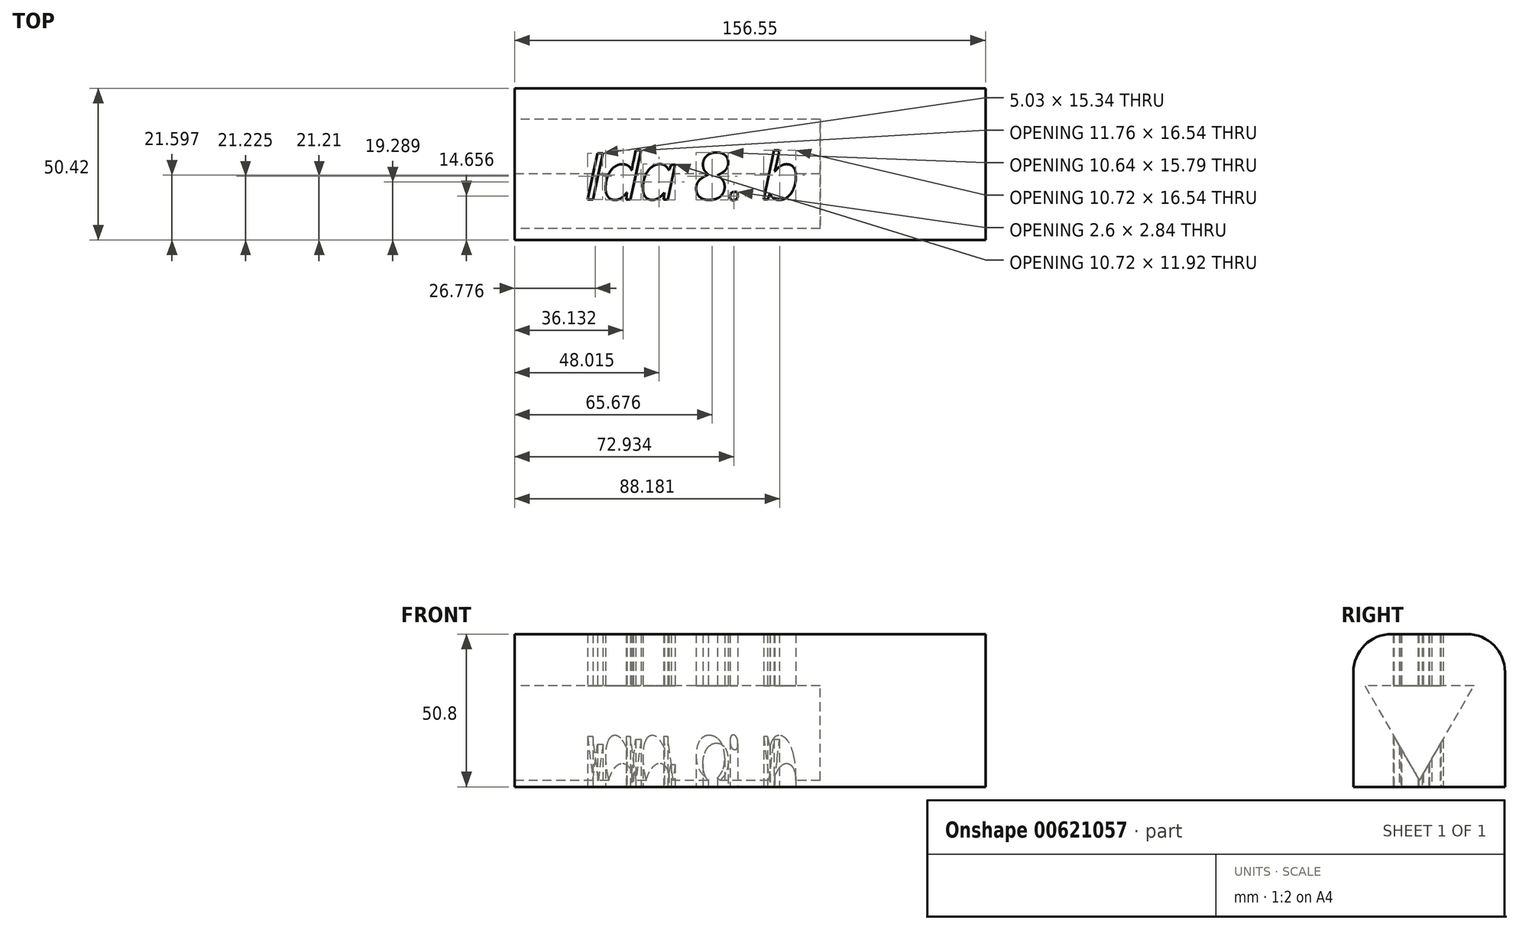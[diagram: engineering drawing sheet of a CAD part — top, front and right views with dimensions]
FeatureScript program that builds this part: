
annotation { "Feature Type Name" : "Feature", "Feature Type Description" : "" }
export const myFeature = defineFeature(function(context is Context, id is Id, definition is map)
    precondition{}
    {
        {
            var Q0;
            Q0=qCreatedBy(makeId("Top.planeOp"),FACE);
            var sketch = newSketch(context, id + "F0", { "sketchPlane" : qUnion([Q0])});
            skLineSegment(sketch, "E0.bottom", {"start": v(16.64, 0) * mm, "end": v(-139.9, 0) * mm});
            skLineSegment(sketch, "E0.top", {"start": v(16.64, 50.42) * mm, "end": v(-139.9, 50.42) * mm});
            skLineSegment(sketch, "E0.left", {"start": v(16.64, 0) * mm, "end": v(16.64, 50.42) * mm});
            skLineSegment(sketch, "E0.right", {"start": v(-139.9, 0) * mm, "end": v(-139.9, 50.42) * mm});
            skPoint(sketch, "E0.middle", {"position": v(-61.63, 25.21) * mm});
            skText(sketch, "E1", { "text": "Ida 8. b", "fontName": "OpenSans-Italic.ttf"});
            const initialGuessF0  = {"E1": [-0.11655, 0.01354, 1, 0, 0.01547]};
            skSetInitialGuess(sketch, initialGuessF0);
            skSolve(sketch);
        }
        {
            var Q0;
            Q0=makeQuery(id+"F0.imprint","IMPRINT",FACE,{"disambiguationData":[TD([[makeQuery(id+"F0.imprint","IMPRINT",EDGE,{"derivedFrom":sQuery(id+"F0.wireOp",EDGE,"E0.bottom")}),-1.0]])]});
            extrude(context, id + "F1", {"entities" : qUnion([Q0]), "depth" : 50.8 * mm, "offsetDistance" : 25.4 * mm});
        }
        {
            var Q0;
            Q0=makeQuery(id+"F1.opExtrude","CAP_EDGE",EDGE,{"disambiguationData":[OSD([sQuery(id+"F0.wireOp",EDGE,"E0.top")])],"isStart":false});
            var Q1;
            Q1=makeQuery(id+"F1.opExtrude","CAP_EDGE",EDGE,{"disambiguationData":[OSD([sQuery(id+"F0.wireOp",EDGE,"E0.bottom")])],"isStart":false});
            fillet(context, id + "F2", {"entities" : qUnion([Q0, Q1]), "radius" : 12.7 * mm, "tangentPropagation" : true, "allowEdgeOverflow" : false});
        }
        {
            var Q0;
            Q0=makeQuery(id+"F1.opExtrude","SWEPT_FACE",FACE,{"disambiguationData":[OSD([sQuery(id+"F0.wireOp",EDGE,"E0.right")])]});
            var sketch = newSketch(context, id + "F3", { "sketchPlane" : qUnion([Q0])});
            skCircle(sketch, "E2.cCircle", {"center": v(-21.96, 23.12) * mm, "radius": 10.5 * mm, "construction": true});
            skLineSegment(sketch, "E2.0", {"start": v(-40.13, 33.61) * mm, "end": v(-3.8, 33.61) * mm});
            skLineSegment(sketch, "E2.1", {"start": v(-3.8, 33.61) * mm, "end": v(-21.96, 2.14) * mm});
            skLineSegment(sketch, "E2.2", {"start": v(-21.96, 2.14) * mm, "end": v(-40.13, 33.61) * mm});
            skPoint(sketch, "E2.0.midPoint", {"position": v(-21.96, 33.61) * mm});
            skSolve(sketch);
        }
        {
            var Q0;
            Q0=makeQuery(id+"F3.imprint","IMPRINT",FACE,{"disambiguationData":[TD([[makeQuery(id+"F3.imprint","IMPRINT",EDGE,{"derivedFrom":sQuery(id+"F3.wireOp",EDGE,"E2.0")}),-1.0]])]});
            extrude(context, id + "F4", {"entities" : qUnion([Q0]), "operationType" : NewBodyOperationType.REMOVE, "oppositeDirection" : true, "depth" : 101.6 * mm, "offsetDistance" : 25.4 * mm});
        }
    });
